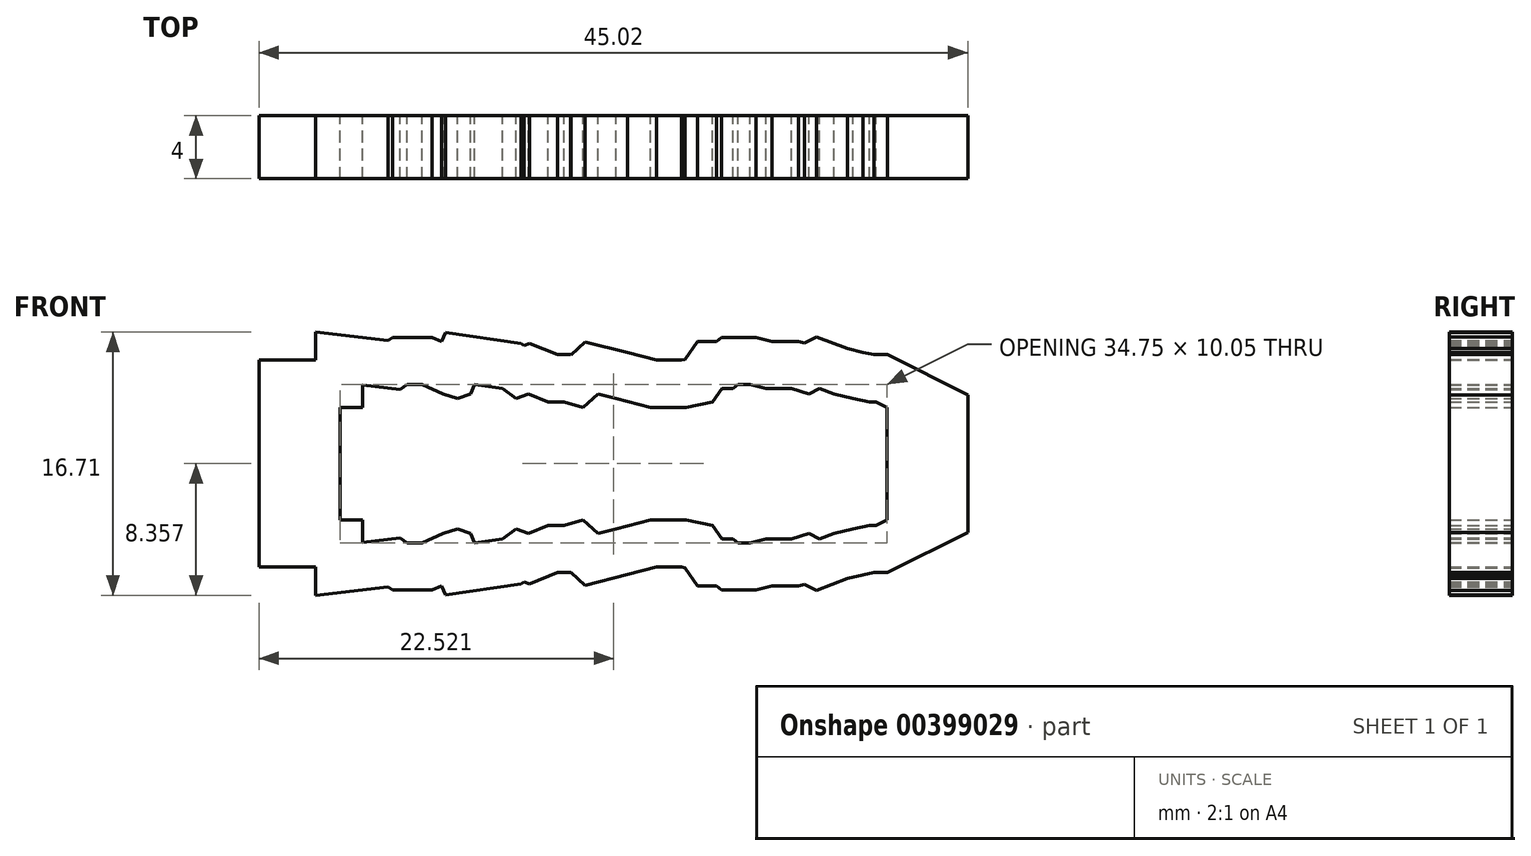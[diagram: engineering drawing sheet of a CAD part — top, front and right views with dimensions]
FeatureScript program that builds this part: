
annotation { "Feature Type Name" : "Feature", "Feature Type Description" : "" }
export const myFeature = defineFeature(function(context is Context, id is Id, definition is map)
    precondition{}
    {
        {
            var Q0;
            Q0=qCreatedBy(makeId("Front.planeOp"),FACE);
            var sketch = newSketch(context, id + "F0", { "sketchPlane" : qUnion([Q0])});
            skLineSegment(sketch, "E0", {"start": v(-12.01, -3.28) * mm, "end": v(24.47, -3.28) * mm, "construction": true});
            skLineSegment(sketch, "E1", {"start": v(-11.73, 0.29) * mm, "end": v(-10.3, 0.29) * mm});
            skLineSegment(sketch, "E2", {"start": v(-10.3, 0.29) * mm, "end": v(-10.3, 1.71) * mm});
            skLineSegment(sketch, "E3", {"start": v(-7.93, 1.44) * mm, "end": v(-7.48, 1.74) * mm});
            skLineSegment(sketch, "E4", {"start": v(-7.48, 1.74) * mm, "end": v(-6.53, 1.74) * mm});
            skLineSegment(sketch, "E5", {"start": v(-6.53, 1.74) * mm, "end": v(-5.2, 1.14) * mm});
            skLineSegment(sketch, "E6", {"start": v(-5.2, 1.14) * mm, "end": v(-4.28, 0.86) * mm});
            skLineSegment(sketch, "E7", {"start": v(-4.28, 0.86) * mm, "end": v(-3.43, 1.14) * mm});
            skLineSegment(sketch, "E8", {"start": v(-3.43, 1.14) * mm, "end": v(-3.18, 1.74) * mm});
            skLineSegment(sketch, "E9", {"start": v(-3.18, 1.74) * mm, "end": v(-1.4, 1.5) * mm});
            skLineSegment(sketch, "E10", {"start": v(-1.4, 1.5) * mm, "end": v(-0.55, 0.86) * mm});
            skLineSegment(sketch, "E11", {"start": v(-0.55, 0.86) * mm, "end": v(0.24, 1.14) * mm});
            skLineSegment(sketch, "E12", {"start": v(0.24, 1.14) * mm, "end": v(1.48, 0.64) * mm});
            skLineSegment(sketch, "E13", {"start": v(1.48, 0.64) * mm, "end": v(2.5, 0.64) * mm});
            skLineSegment(sketch, "E14", {"start": v(2.5, 0.64) * mm, "end": v(3.7, 0.29) * mm});
            skLineSegment(sketch, "E15", {"start": v(3.7, 0.29) * mm, "end": v(4.65, 1.14) * mm});
            skLineSegment(sketch, "E16", {"start": v(4.65, 1.14) * mm, "end": v(5.79, 0.86) * mm});
            skLineSegment(sketch, "E17", {"start": v(5.79, 0.86) * mm, "end": v(7.97, 0.29) * mm});
            skLineSegment(sketch, "E18", {"start": v(7.97, 0.29) * mm, "end": v(9.71, 0.29) * mm});
            skLineSegment(sketch, "E19", {"start": v(9.71, 0.29) * mm, "end": v(10.25, 0.29) * mm});
            skLineSegment(sketch, "E20", {"start": v(10.25, 0.29) * mm, "end": v(11.93, 0.64) * mm});
            skLineSegment(sketch, "E21", {"start": v(11.93, 0.64) * mm, "end": v(12.53, 1.5) * mm});
            skLineSegment(sketch, "E22", {"start": v(12.53, 1.5) * mm, "end": v(13.23, 1.5) * mm});
            skLineSegment(sketch, "E23", {"start": v(13.23, 1.5) * mm, "end": v(13.55, 1.74) * mm});
            skLineSegment(sketch, "E24", {"start": v(13.55, 1.74) * mm, "end": v(14.3, 1.74) * mm});
            skLineSegment(sketch, "E25", {"start": v(15.32, 1.5) * mm, "end": v(16.93, 1.5) * mm});
            skLineSegment(sketch, "E26", {"start": v(16.93, 1.5) * mm, "end": v(18.04, 1.14) * mm});
            skLineSegment(sketch, "E27", {"start": v(18.04, 1.14) * mm, "end": v(18.7, 1.5) * mm});
            skLineSegment(sketch, "E28", {"start": v(19.63, 1.14) * mm, "end": v(20.83, 0.86) * mm});
            skLineSegment(sketch, "E29", {"start": v(20.83, 0.86) * mm, "end": v(21.88, 0.64) * mm});
            skLineSegment(sketch, "E30", {"start": v(21.88, 0.64) * mm, "end": v(22.32, 0.64) * mm});
            skLineSegment(sketch, "E31", {"start": v(22.32, 0.64) * mm, "end": v(23.02, 0.29) * mm});
            skPoint(sketch, "E32.end.orphan", {"position": v(19.16, 0.64) * mm});
            skLineSegment(sketch, "E33", {"start": v(18.7, 1.5) * mm, "end": v(19.63, 1.14) * mm});
            skPoint(sketch, "E34.end.orphan", {"position": v(14.78, 0.86) * mm});
            skLineSegment(sketch, "E35", {"start": v(14.3, 1.74) * mm, "end": v(15.32, 1.5) * mm});
            skLineSegment(sketch, "E36", {"start": v(-10.3, 1.71) * mm, "end": v(-7.93, 1.44) * mm});
            skPoint(sketch, "E37.orphan", {"position": v(-8.37, 1.14) * mm});
            skLineSegment(sketch, "E38.0", {"start": v(23.03, 3.64) * mm, "end": v(28.14, 1.08) * mm});
            skLineSegment(sketch, "E38.1", {"start": v(22.2, 3.64) * mm, "end": v(23.03, 3.64) * mm});
            skLineSegment(sketch, "E38.2", {"start": v(21.49, 3.78) * mm, "end": v(22.2, 3.64) * mm});
            skLineSegment(sketch, "E38.3", {"start": v(20.5, 4.02) * mm, "end": v(21.49, 3.78) * mm});
            skLineSegment(sketch, "E38.4", {"start": v(18.51, 4.77) * mm, "end": v(20.5, 4.02) * mm});
            skLineSegment(sketch, "E38.5", {"start": v(17.75, 4.38) * mm, "end": v(18.51, 4.77) * mm});
            skLineSegment(sketch, "E38.6", {"start": v(17.4, 4.5) * mm, "end": v(17.75, 4.38) * mm});
            skLineSegment(sketch, "E38.7", {"start": v(15.69, 4.5) * mm, "end": v(17.4, 4.5) * mm});
            skLineSegment(sketch, "E38.8", {"start": v(14.68, 4.74) * mm, "end": v(15.69, 4.5) * mm});
            skLineSegment(sketch, "E38.9", {"start": v(12.5, 4.74) * mm, "end": v(14.68, 4.74) * mm});
            skLineSegment(sketch, "E38.10", {"start": v(12.18, 4.5) * mm, "end": v(12.5, 4.74) * mm});
            skLineSegment(sketch, "E38.11", {"start": v(-0.23, 4.35) * mm, "end": v(-0.05, 4.22) * mm});
            skLineSegment(sketch, "E38.12", {"start": v(-5.04, 5.04) * mm, "end": v(-0.23, 4.35) * mm});
            skLineSegment(sketch, "E38.13", {"start": v(-5.28, 4.47) * mm, "end": v(-5.04, 5.04) * mm});
            skLineSegment(sketch, "E38.14", {"start": v(-5.89, 4.74) * mm, "end": v(-5.28, 4.47) * mm});
            skLineSegment(sketch, "E38.15", {"start": v(-8.4, 4.74) * mm, "end": v(-5.89, 4.74) * mm});
            skLineSegment(sketch, "E38.16", {"start": v(-8.7, 4.55) * mm, "end": v(-8.4, 4.74) * mm});
            skLineSegment(sketch, "E38.17", {"start": v(-16.88, 3.29) * mm, "end": v(-16.88, -0.28) * mm});
            skLineSegment(sketch, "E38.18", {"start": v(-16.88, 3.29) * mm, "end": v(-13.3, 3.29) * mm});
            skLineSegment(sketch, "E38.19", {"start": v(-13.3, 3.29) * mm, "end": v(-13.3, 5.07) * mm});
            skLineSegment(sketch, "E38.20", {"start": v(-13.3, 5.07) * mm, "end": v(-8.7, 4.55) * mm});
            skLineSegment(sketch, "E38.21", {"start": v(-0.05, 4.22) * mm, "end": v(0.31, 4.36) * mm});
            skLineSegment(sketch, "E38.22", {"start": v(0.31, 4.36) * mm, "end": v(2.07, 3.64) * mm});
            skLineSegment(sketch, "E38.23", {"start": v(2.07, 3.64) * mm, "end": v(2.92, 3.64) * mm});
            skLineSegment(sketch, "E38.24", {"start": v(2.92, 3.64) * mm, "end": v(2.93, 3.63) * mm});
            skLineSegment(sketch, "E38.25", {"start": v(2.93, 3.63) * mm, "end": v(3.83, 4.44) * mm});
            skLineSegment(sketch, "E38.26", {"start": v(3.83, 4.44) * mm, "end": v(6.53, 3.76) * mm});
            skLineSegment(sketch, "E38.27", {"start": v(6.53, 3.76) * mm, "end": v(8.36, 3.29) * mm});
            skLineSegment(sketch, "E38.28", {"start": v(8.36, 3.29) * mm, "end": v(9.71, 3.29) * mm});
            skLineSegment(sketch, "E38.29", {"start": v(9.71, 3.29) * mm, "end": v(9.94, 3.29) * mm});
            skLineSegment(sketch, "E38.30", {"start": v(9.94, 3.29) * mm, "end": v(10.16, 3.33) * mm});
            skLineSegment(sketch, "E38.31", {"start": v(10.16, 3.33) * mm, "end": v(10.98, 4.5) * mm});
            skLineSegment(sketch, "E38.32", {"start": v(10.98, 4.5) * mm, "end": v(12.18, 4.5) * mm});
            skLineSegment(sketch, "E39.MirrorCS", {"start": v(2.92, -10.2) * mm, "end": v(2.93, -10.2) * mm});
            skLineSegment(sketch, "E40.MirrorCS", {"start": v(9.71, -9.85) * mm, "end": v(9.94, -9.85) * mm});
            skLineSegment(sketch, "E41.MirrorCS", {"start": v(9.94, -9.85) * mm, "end": v(10.16, -9.9) * mm});
            skLineSegment(sketch, "E42.MirrorCS", {"start": v(14.68, -11.3) * mm, "end": v(15.69, -11.06) * mm});
            skLineSegment(sketch, "E43.MirrorCS", {"start": v(18.7, -8.06) * mm, "end": v(19.63, -7.7) * mm});
            skLineSegment(sketch, "E44.MirrorCS", {"start": v(1.48, -7.2) * mm, "end": v(2.5, -7.2) * mm});
            skLineSegment(sketch, "E45.MirrorCS", {"start": v(13.55, -8.3) * mm, "end": v(14.3, -8.3) * mm});
            skLineSegment(sketch, "E46.MirrorCS", {"start": v(12.53, -8.06) * mm, "end": v(13.23, -8.06) * mm});
            skLineSegment(sketch, "E47.MirrorCS", {"start": v(-8.7, -11.11) * mm, "end": v(-8.4, -11.3) * mm});
            skLineSegment(sketch, "E48.MirrorCS", {"start": v(-3.43, -7.7) * mm, "end": v(-3.18, -8.3) * mm});
            skLineSegment(sketch, "E49.MirrorCS", {"start": v(21.88, -7.2) * mm, "end": v(22.32, -7.2) * mm});
            skLineSegment(sketch, "E50.MirrorCS", {"start": v(20.5, -10.58) * mm, "end": v(21.49, -10.35) * mm});
            skLineSegment(sketch, "E51.MirrorCS", {"start": v(-0.23, -10.92) * mm, "end": v(-0.05, -10.79) * mm});
            skLineSegment(sketch, "E52.MirrorCS", {"start": v(22.2, -10.2) * mm, "end": v(23.03, -10.2) * mm});
            skLineSegment(sketch, "E53.MirrorCS", {"start": v(18.04, -7.7) * mm, "end": v(18.7, -8.06) * mm});
            skLineSegment(sketch, "E54.MirrorCS", {"start": v(21.49, -10.35) * mm, "end": v(22.2, -10.2) * mm});
            skLineSegment(sketch, "E55.MirrorCS", {"start": v(-7.48, -8.3) * mm, "end": v(-6.53, -8.3) * mm});
            skLineSegment(sketch, "E56.MirrorCS", {"start": v(16.93, -8.06) * mm, "end": v(18.04, -7.7) * mm});
            skLineSegment(sketch, "E57.MirrorCS", {"start": v(-5.2, -7.7) * mm, "end": v(-4.28, -7.42) * mm});
            skLineSegment(sketch, "E58.MirrorCS", {"start": v(-0.05, -10.79) * mm, "end": v(0.31, -10.92) * mm});
            skLineSegment(sketch, "E59.MirrorCS", {"start": v(17.4, -11.06) * mm, "end": v(17.75, -10.94) * mm});
            skLineSegment(sketch, "E60.MirrorCS", {"start": v(-4.28, -7.42) * mm, "end": v(-3.43, -7.7) * mm});
            skLineSegment(sketch, "E61.MirrorCS", {"start": v(13.23, -8.06) * mm, "end": v(13.55, -8.3) * mm});
            skLineSegment(sketch, "E62.MirrorCS", {"start": v(-5.89, -11.3) * mm, "end": v(-5.28, -11.04) * mm});
            skLineSegment(sketch, "E63.MirrorCS", {"start": v(2.07, -10.2) * mm, "end": v(2.92, -10.2) * mm});
            skLineSegment(sketch, "E64.MirrorCS", {"start": v(14.3, -8.3) * mm, "end": v(15.32, -8.06) * mm});
            skLineSegment(sketch, "E65.MirrorCS", {"start": v(11.93, -7.2) * mm, "end": v(12.53, -8.06) * mm});
            skLineSegment(sketch, "E66.MirrorCS", {"start": v(9.71, -6.85) * mm, "end": v(10.25, -6.85) * mm});
            skLineSegment(sketch, "E67.MirrorCS", {"start": v(-1.4, -8.06) * mm, "end": v(-0.55, -7.42) * mm});
            skLineSegment(sketch, "E68.MirrorCS", {"start": v(-7.93, -8) * mm, "end": v(-7.48, -8.3) * mm});
            skLineSegment(sketch, "E69.MirrorCS", {"start": v(17.75, -10.94) * mm, "end": v(18.51, -11.34) * mm});
            skLineSegment(sketch, "E70.MirrorCS", {"start": v(-5.28, -11.04) * mm, "end": v(-5.04, -11.6) * mm});
            skLineSegment(sketch, "E71.MirrorCS", {"start": v(2.93, -10.2) * mm, "end": v(3.83, -11) * mm});
            skLineSegment(sketch, "E72.MirrorCS", {"start": v(3.7, -6.85) * mm, "end": v(4.65, -7.7) * mm});
            skLineSegment(sketch, "E73.MirrorCS", {"start": v(20.83, -7.42) * mm, "end": v(21.88, -7.2) * mm});
            skLineSegment(sketch, "E74.MirrorCS", {"start": v(12.18, -11.06) * mm, "end": v(12.5, -11.3) * mm});
            skLineSegment(sketch, "E75.MirrorCS", {"start": v(-0.55, -7.42) * mm, "end": v(0.24, -7.7) * mm});
            skLineSegment(sketch, "E76.MirrorCS", {"start": v(22.32, -7.2) * mm, "end": v(23.02, -6.85) * mm});
            skLineSegment(sketch, "E77.MirrorCS", {"start": v(-8.4, -11.3) * mm, "end": v(-5.89, -11.3) * mm});
            skPoint(sketch, "E78.MirrorP", {"position": v(19.16, -7.2) * mm});
            skLineSegment(sketch, "E79.MirrorCS", {"start": v(23.03, -10.2) * mm, "end": v(28.14, -7.64) * mm});
            skLineSegment(sketch, "E80.MirrorCS", {"start": v(-10.3, -6.85) * mm, "end": v(-10.3, -8.28) * mm});
            skLineSegment(sketch, "E81.MirrorCS", {"start": v(6.53, -10.33) * mm, "end": v(8.36, -9.85) * mm});
            skLineSegment(sketch, "E82.MirrorCS", {"start": v(15.69, -11.06) * mm, "end": v(17.4, -11.06) * mm});
            skLineSegment(sketch, "E83.MirrorCS", {"start": v(10.98, -11.06) * mm, "end": v(12.18, -11.06) * mm});
            skLineSegment(sketch, "E84.MirrorCS", {"start": v(10.16, -9.9) * mm, "end": v(10.98, -11.06) * mm});
            skLineSegment(sketch, "E85.MirrorCS", {"start": v(-13.3, -11.64) * mm, "end": v(-8.7, -11.11) * mm});
            skLineSegment(sketch, "E86.MirrorCS", {"start": v(0.31, -10.92) * mm, "end": v(2.07, -10.2) * mm});
            skPoint(sketch, "E87.MirrorP", {"position": v(-8.37, -7.7) * mm});
            skLineSegment(sketch, "E88.MirrorCS", {"start": v(-16.88, -9.85) * mm, "end": v(-13.3, -9.85) * mm});
            skLineSegment(sketch, "E89.MirrorCS", {"start": v(0.24, -7.7) * mm, "end": v(1.48, -7.2) * mm});
            skLineSegment(sketch, "E90.MirrorCS", {"start": v(2.5, -7.2) * mm, "end": v(3.7, -6.85) * mm});
            skLineSegment(sketch, "E91.MirrorCS", {"start": v(-11.73, -6.85) * mm, "end": v(-10.3, -6.85) * mm});
            skLineSegment(sketch, "E92.MirrorCS", {"start": v(18.51, -11.34) * mm, "end": v(20.5, -10.58) * mm});
            skLineSegment(sketch, "E93.MirrorCS", {"start": v(-6.53, -8.3) * mm, "end": v(-5.2, -7.7) * mm});
            skLineSegment(sketch, "E94.MirrorCS", {"start": v(-3.18, -8.3) * mm, "end": v(-1.4, -8.06) * mm});
            skLineSegment(sketch, "E95.MirrorCS", {"start": v(-5.04, -11.6) * mm, "end": v(-0.23, -10.92) * mm});
            skLineSegment(sketch, "E96.MirrorCS", {"start": v(19.63, -7.7) * mm, "end": v(20.83, -7.42) * mm});
            skLineSegment(sketch, "E97.MirrorCS", {"start": v(-10.3, -8.28) * mm, "end": v(-7.93, -8) * mm});
            skLineSegment(sketch, "E98.MirrorCS", {"start": v(7.97, -6.85) * mm, "end": v(9.71, -6.85) * mm});
            skLineSegment(sketch, "E99.MirrorCS", {"start": v(12.5, -11.3) * mm, "end": v(14.68, -11.3) * mm});
            skLineSegment(sketch, "E100.MirrorCS", {"start": v(15.32, -8.06) * mm, "end": v(16.93, -8.06) * mm});
            skLineSegment(sketch, "E101.MirrorCS", {"start": v(-16.88, -9.85) * mm, "end": v(-16.88, -6.28) * mm});
            skLineSegment(sketch, "E102.MirrorCS", {"start": v(5.79, -7.42) * mm, "end": v(7.97, -6.85) * mm});
            skLineSegment(sketch, "E103.MirrorCS", {"start": v(3.83, -11) * mm, "end": v(6.53, -10.33) * mm});
            skPoint(sketch, "E104.MirrorP", {"position": v(14.78, -7.42) * mm});
            skLineSegment(sketch, "E105.MirrorCS", {"start": v(4.65, -7.7) * mm, "end": v(5.79, -7.42) * mm});
            skLineSegment(sketch, "E106.MirrorCS", {"start": v(10.25, -6.85) * mm, "end": v(11.93, -7.2) * mm});
            skLineSegment(sketch, "E107.MirrorCS", {"start": v(-13.3, -9.85) * mm, "end": v(-13.3, -11.64) * mm});
            skLineSegment(sketch, "E108.MirrorCS", {"start": v(8.36, -9.85) * mm, "end": v(9.71, -9.85) * mm});
            skLineSegment(sketch, "E109", {"start": v(23.02, 0.29) * mm, "end": v(23.02, -6.85) * mm});
            skLineSegment(sketch, "E110", {"start": v(28.14, -7.64) * mm, "end": v(28.14, 1.08) * mm});
            skLineSegment(sketch, "E111", {"start": v(-16.88, -0.28) * mm, "end": v(-16.88, -6.28) * mm});
            skLineSegment(sketch, "E112", {"start": v(-11.73, 0.29) * mm, "end": v(-11.73, -6.85) * mm});
            skPoint(sketch, "E113.orphan", {"position": v(-13.17, 0.29) * mm});
            skPoint(sketch, "E114.orphan", {"position": v(-13.17, -6.85) * mm});
            skSolve(sketch);
        }
        {
            var Q0;
            Q0=makeQuery(id+"F0.imprint","IMPRINT",FACE,{"disambiguationData":[TD([[makeQuery(id+"F0.imprint","IMPRINT",EDGE,{"derivedFrom":sQuery(id+"F0.wireOp",EDGE,"E1")}),1.0]])]});
            extrude(context, id + "F1", {"entities" : qUnion([Q0]), "depth" : 4 * mm});
        }
    });
